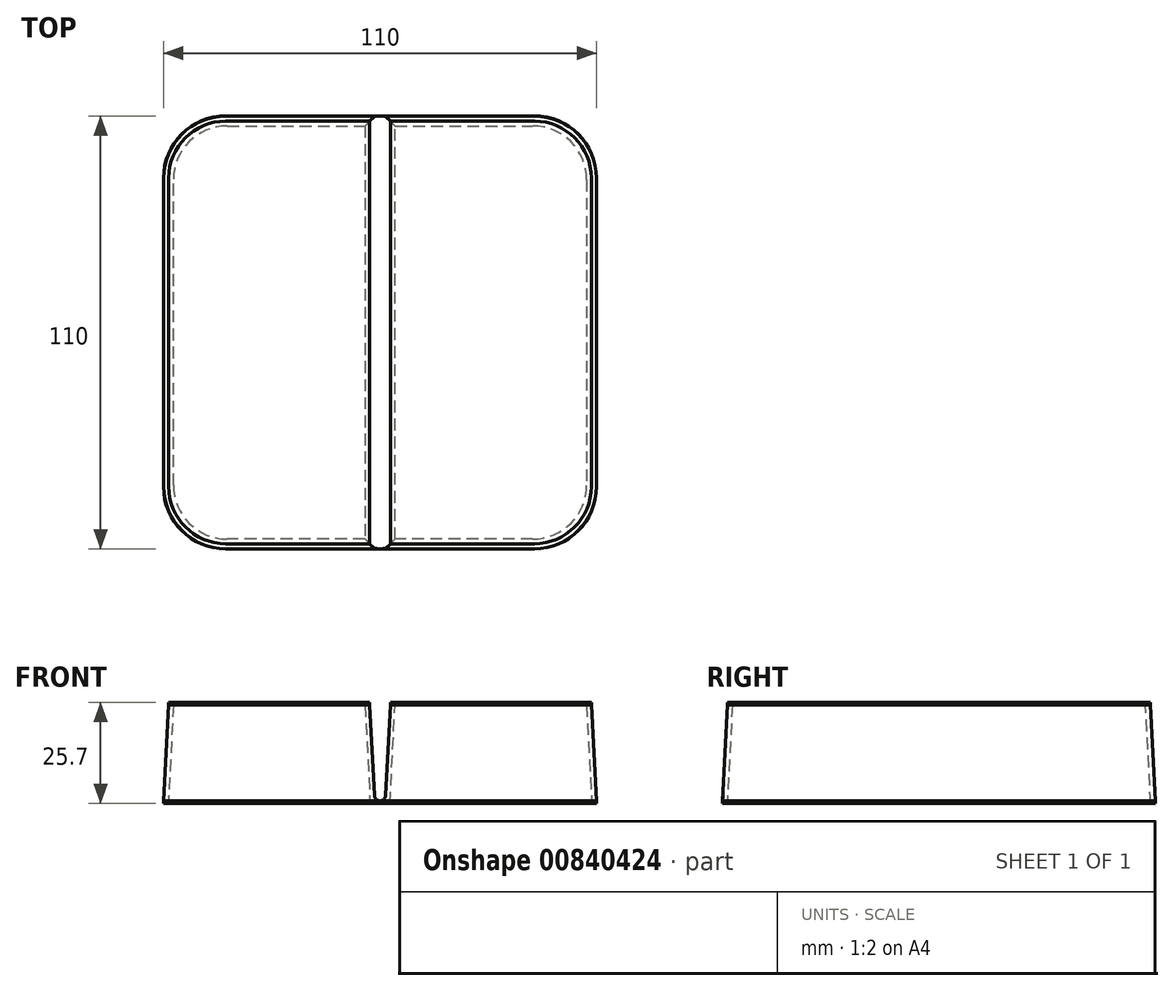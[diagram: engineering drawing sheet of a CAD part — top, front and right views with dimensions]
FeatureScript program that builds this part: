
annotation { "Feature Type Name" : "Feature", "Feature Type Description" : "" }
export const myFeature = defineFeature(function(context is Context, id is Id, definition is map)
    precondition{}
    {
        {
            var Q0;
            Q0=qCreatedBy(makeId("Top.planeOp"),FACE);
            var sketch = newSketch(context, id + "F0", { "sketchPlane" : qUnion([Q0])});
            skLineSegment(sketch, "E0.bottom", {"start": v(-39.2, 55) * mm, "end": v(39.2, 55) * mm});
            skLineSegment(sketch, "E0.top", {"start": v(-39.2, -55) * mm, "end": v(39.2, -55) * mm});
            skLineSegment(sketch, "E0.left", {"start": v(-55, 39.2) * mm, "end": v(-55, -39.2) * mm});
            skLineSegment(sketch, "E0.right", {"start": v(55, 39.2) * mm, "end": v(55, -39.2) * mm});
            skPoint(sketch, "E0.middle", {"position": v(0, 0) * mm});
            skLineSegment(sketch, "E1.bottom", {"start": v(39.2, 65) * mm, "end": v(-39.2, 65) * mm});
            skLineSegment(sketch, "E1.top", {"start": v(39.2, -65) * mm, "end": v(-39.2, -65) * mm});
            skLineSegment(sketch, "E1.left", {"start": v(65, 39.2) * mm, "end": v(65, -39.2) * mm});
            skLineSegment(sketch, "E1.right", {"start": v(-65, 39.2) * mm, "end": v(-65, -39.2) * mm});
            skLineSegment(sketch, "E2.0", {"start": v(-38.8, 53.8) * mm, "end": v(38.8, 53.8) * mm});
            skLineSegment(sketch, "E2.1", {"start": v(-53.8, 38.8) * mm, "end": v(-53.8, -38.8) * mm});
            skLineSegment(sketch, "E2.2", {"start": v(-38.8, -53.8) * mm, "end": v(38.8, -53.8) * mm});
            skLineSegment(sketch, "E2.3", {"start": v(53.8, 38.8) * mm, "end": v(53.8, -38.8) * mm});
            skPoint(sketch, "E3.visualSharp", {"position": v(-53.8, -53.8) * mm});
            skArc(sketch, "E3.filletArc", {"start": v(-53.8, -38.8) * mm, "mid": v(-49.4, -49.4) * mm, "end": v(-38.8, -53.8) * mm});
            skPoint(sketch, "E4.visualSharp", {"position": v(-55, -55) * mm});
            skArc(sketch, "E4.filletArc", {"start": v(-55, -39.2) * mm, "mid": v(-50.37, -50.37) * mm, "end": v(-39.2, -55) * mm});
            skPoint(sketch, "E5.visualSharp", {"position": v(53.8, -53.8) * mm});
            skArc(sketch, "E5.filletArc", {"start": v(38.8, -53.8) * mm, "mid": v(49.4, -49.4) * mm, "end": v(53.8, -38.8) * mm});
            skPoint(sketch, "E6.visualSharp", {"position": v(53.8, 53.8) * mm});
            skArc(sketch, "E6.filletArc", {"start": v(53.8, 38.8) * mm, "mid": v(49.4, 49.4) * mm, "end": v(38.8, 53.8) * mm});
            skPoint(sketch, "E7.visualSharp", {"position": v(-53.8, 53.8) * mm});
            skArc(sketch, "E7.filletArc", {"start": v(-38.8, 53.8) * mm, "mid": v(-49.4, 49.4) * mm, "end": v(-53.8, 38.8) * mm});
            skPoint(sketch, "E8.visualSharp", {"position": v(-55, 55) * mm});
            skArc(sketch, "E8.filletArc", {"start": v(-39.2, 55) * mm, "mid": v(-50.37, 50.37) * mm, "end": v(-55, 39.2) * mm});
            skPoint(sketch, "E9.visualSharp", {"position": v(55, 55) * mm});
            skArc(sketch, "E9.filletArc", {"start": v(55, 39.2) * mm, "mid": v(50.37, 50.37) * mm, "end": v(39.2, 55) * mm});
            skPoint(sketch, "E10.visualSharp", {"position": v(55, -55) * mm});
            skArc(sketch, "E10.filletArc", {"start": v(39.2, -55) * mm, "mid": v(50.37, -50.37) * mm, "end": v(55, -39.2) * mm});
            skPoint(sketch, "E11.visualSharp", {"position": v(65, -65) * mm});
            skArc(sketch, "E11.filletArc", {"start": v(39.2, -65) * mm, "mid": v(57.44, -57.44) * mm, "end": v(65, -39.2) * mm});
            skPoint(sketch, "E12.visualSharp", {"position": v(-65, -65) * mm});
            skArc(sketch, "E12.filletArc", {"start": v(-65, -39.2) * mm, "mid": v(-57.44, -57.44) * mm, "end": v(-39.2, -65) * mm});
            skPoint(sketch, "E13.visualSharp", {"position": v(65, 65) * mm});
            skArc(sketch, "E13.filletArc", {"start": v(65, 39.2) * mm, "mid": v(57.44, 57.44) * mm, "end": v(39.2, 65) * mm});
            skPoint(sketch, "E14.visualSharp", {"position": v(-65, 65) * mm});
            skArc(sketch, "E14.filletArc", {"start": v(-39.2, 65) * mm, "mid": v(-57.44, 57.44) * mm, "end": v(-65, 39.2) * mm});
            skLineSegment(sketch, "E15.0", {"start": v(60, 35.37) * mm, "end": v(60, -43.03) * mm});
            skLineSegment(sketch, "E16.0", {"start": v(-60, 35.37) * mm, "end": v(-60, -43.03) * mm});
            skCircle(sketch, "E17", {"center": v(60, 35.37) * mm, "radius": 2.1 * mm});
            skCircle(sketch, "E18", {"center": v(60, -43.03) * mm, "radius": 2.1 * mm});
            skCircle(sketch, "E19", {"center": v(-60, 35.37) * mm, "radius": 2.1 * mm});
            skCircle(sketch, "E20", {"center": v(-60, -43.03) * mm, "radius": 2.1 * mm});
            skLineSegment(sketch, "E21.0", {"start": v(39.2, 60) * mm, "end": v(-39.2, 60) * mm});
            skCircle(sketch, "E22", {"center": v(-39.2, 60) * mm, "radius": 2.1 * mm});
            skCircle(sketch, "E23", {"center": v(39.2, 60) * mm, "radius": 2.1 * mm});
            skLineSegment(sketch, "E24", {"start": v(-2.5, -55) * mm, "end": v(-2.5, 55) * mm});
            skLineSegment(sketch, "E25", {"start": v(2.5, 55) * mm, "end": v(2.5, -55) * mm});
            skLineSegment(sketch, "E26.0", {"start": v(1.3, 55) * mm, "end": v(1.3, -55) * mm});
            skLineSegment(sketch, "E27.0", {"start": v(-1.3, -55) * mm, "end": v(-1.3, 55) * mm});
            skSolve(sketch);
        }
        {
            var Q0;
            Q0=makeQuery(id+"F0.imprint","IMPRINT",FACE,{"disambiguationData":[TD([[makeQuery(id+"F0.imprint","IMPRINT",EDGE,{"derivedFrom":sQuery(id+"F0.wireOp",EDGE,"E0.bottom")}),-1.0]])]});
            var Q1;
            {var subQ0=sQuery(id+"F0.wireOp",EDGE,"E24");Q1=makeQuery(id+"F0.imprint","IMPRINT",FACE,{"disambiguationData":[TD([[makeQuery(id+"F0.imprint","IMPRINT",EDGE,{"derivedFrom":subQ0}),-1.0]])]});}
            var Q2;
            {var subQ0=sQuery(id+"F0.wireOp",EDGE,"E25");var subQ1=sQuery(id+"F0.wireOp",EDGE,"E2.0");var subQ2=makeQuery(id+"F0.imprint","INTERSECT",VERTEX,{"derivedFrom":[subQ1,subQ0]});Q2=makeQuery(id+"F0.imprint","IMPRINT",FACE,{"disambiguationData":[TD([[makeQuery(id+"F0.imprint","IMPRINT",EDGE,{"disambiguationData":[TD([[subQ2,1.0]])],"derivedFrom":subQ1}),-1.0]])]});}
            var Q3;
            {var subQ3=sQuery(id+"F0.wireOp",EDGE,"E27.0");Q3=makeQuery(id+"F0.imprint","IMPRINT",FACE,{"disambiguationData":[TD([[makeQuery(id+"F0.imprint","IMPRINT",EDGE,{"derivedFrom":subQ3}),-1.0]])]});}
            var Q4;
            {var subQ0=sQuery(id+"F0.wireOp",EDGE,"E25");var subQ1=sQuery(id+"F0.wireOp",EDGE,"E0.top");var subQ2=makeQuery(id+"F0.imprint","INTERSECT",VERTEX,{"derivedFrom":[subQ1,subQ0]});Q4=makeQuery(id+"F0.imprint","IMPRINT",FACE,{"disambiguationData":[TD([[makeQuery(id+"F0.imprint","IMPRINT",EDGE,{"disambiguationData":[TD([[subQ2,1.0]])],"derivedFrom":subQ1}),1.0]])]});}
            var Q5;
            Q5=makeQuery(id+"F0.imprint","IMPRINT",FACE,{"disambiguationData":[TD([[makeQuery(id+"F0.imprint","IMPRINT",EDGE,{"derivedFrom":sQuery(id+"F0.wireOp",EDGE,"E0.right")}),-1.0]])]});
            var Q6;
            Q6=makeQuery(id+"F0.imprint","IMPRINT",FACE,{"disambiguationData":[TD([[makeQuery(id+"F0.imprint","IMPRINT",EDGE,{"derivedFrom":sQuery(id+"F0.wireOp",EDGE,"E0.left")}),1.0]])]});
            extrude(context, id + "F1", {"entities" : qUnion([Q0, Q1, Q2, Q3, Q4, Q5, Q6]), "depth" : 0.7 * mm, "offsetDistance" : 25 * mm});
        }
        {
            var Q0;
            {var subQ0=sQuery(id+"F0.wireOp",EDGE,"E25");var subQ1=sQuery(id+"F0.wireOp",EDGE,"E0.bottom");var subQ2=makeQuery(id+"F0.imprint","INTERSECT",VERTEX,{"derivedFrom":[subQ1,subQ0]});Q0=makeQuery(id+"F0.imprint","IMPRINT",FACE,{"disambiguationData":[TD([[makeQuery(id+"F0.imprint","IMPRINT",EDGE,{"disambiguationData":[TD([[subQ2,1.0]])],"derivedFrom":subQ1}),-1.0]])]});}
            var Q1;
            {var subQ0=sQuery(id+"F0.wireOp",EDGE,"E25");var subQ1=sQuery(id+"F0.wireOp",EDGE,"E0.top");var subQ2=makeQuery(id+"F0.imprint","INTERSECT",VERTEX,{"derivedFrom":[subQ1,subQ0]});Q1=makeQuery(id+"F0.imprint","IMPRINT",FACE,{"disambiguationData":[TD([[makeQuery(id+"F0.imprint","IMPRINT",EDGE,{"disambiguationData":[TD([[subQ2,1.0]])],"derivedFrom":subQ1}),1.0]])]});}
            var Q2;
            {var subQ0=sQuery(id+"F0.wireOp",EDGE,"E26.0");var subQ1=sQuery(id+"F0.wireOp",EDGE,"E2.0");var subQ2=makeQuery(id+"F0.imprint","INTERSECT",VERTEX,{"derivedFrom":[subQ1,subQ0]});Q2=makeQuery(id+"F0.imprint","IMPRINT",FACE,{"disambiguationData":[TD([[makeQuery(id+"F0.imprint","IMPRINT",EDGE,{"disambiguationData":[TD([[subQ2,-1.0]])],"derivedFrom":subQ1}),-1.0]])]});}
            var Q3;
            Q3=makeQuery(id+"F0.imprint","IMPRINT",FACE,{"disambiguationData":[TD([[makeQuery(id+"F0.imprint","IMPRINT",EDGE,{"derivedFrom":sQuery(id+"F0.wireOp",EDGE,"E0.right")}),-1.0]])]});
            var Q4;
            Q4=makeQuery(id+"F0.imprint","IMPRINT",FACE,{"disambiguationData":[TD([[makeQuery(id+"F0.imprint","IMPRINT",EDGE,{"derivedFrom":sQuery(id+"F0.wireOp",EDGE,"E2.3")}),-1.0]])]});
            var Q5;
            {var subQ0=sQuery(id+"F0.wireOp",EDGE,"E24");var subQ1=sQuery(id+"F0.wireOp",EDGE,"E2.0");var subQ2=makeQuery(id+"F0.imprint","INTERSECT",VERTEX,{"derivedFrom":[subQ1,subQ0]});Q5=makeQuery(id+"F0.imprint","IMPRINT",FACE,{"disambiguationData":[TD([[makeQuery(id+"F0.imprint","IMPRINT",EDGE,{"disambiguationData":[TD([[subQ2,-1.0]])],"derivedFrom":subQ1}),-1.0]])]});}
            var Q6;
            {var subQ0=sQuery(id+"F0.wireOp",EDGE,"E24");var subQ1=sQuery(id+"F0.wireOp",EDGE,"E0.top");var subQ2=makeQuery(id+"F0.imprint","INTERSECT",VERTEX,{"derivedFrom":[subQ1,subQ0]});Q6=makeQuery(id+"F0.imprint","IMPRINT",FACE,{"disambiguationData":[TD([[makeQuery(id+"F0.imprint","IMPRINT",EDGE,{"disambiguationData":[TD([[subQ2,-1.0]])],"derivedFrom":subQ1}),1.0]])]});}
            var Q7;
            Q7=makeQuery(id+"F0.imprint","IMPRINT",FACE,{"disambiguationData":[TD([[makeQuery(id+"F0.imprint","IMPRINT",EDGE,{"derivedFrom":sQuery(id+"F0.wireOp",EDGE,"E0.left")}),1.0]])]});
            var Q8;
            {var subQ0=sQuery(id+"F0.wireOp",EDGE,"E24");var subQ1=sQuery(id+"F0.wireOp",EDGE,"E0.bottom");var subQ2=makeQuery(id+"F0.imprint","INTERSECT",VERTEX,{"derivedFrom":[subQ1,subQ0]});Q8=makeQuery(id+"F0.imprint","IMPRINT",FACE,{"disambiguationData":[TD([[makeQuery(id+"F0.imprint","IMPRINT",EDGE,{"disambiguationData":[TD([[subQ2,-1.0]])],"derivedFrom":subQ1}),-1.0]])]});}
            var Q9;
            Q9=makeQuery(id+"F0.imprint","IMPRINT",FACE,{"disambiguationData":[TD([[makeQuery(id+"F0.imprint","IMPRINT",EDGE,{"derivedFrom":sQuery(id+"F0.wireOp",EDGE,"E2.1")}),1.0]])]});
            extrude(context, id + "F2", {"entities" : qUnion([Q0, Q1, Q2, Q3, Q4, Q5, Q6, Q7, Q8, Q9]), "operationType" : NewBodyOperationType.ADD, "depth" : 25 * mm, "offsetDistance" : 25 * mm, "hasDraft" : true, "draftAngle" : 3 * degree, "draftPullDirection" : true});
        }
        {
            var Q0;
            Q0=makeQuery(id+"F0.imprint","IMPRINT",FACE,{"disambiguationData":[TD([[makeQuery(id+"F0.imprint","IMPRINT",EDGE,{"derivedFrom":sQuery(id+"F0.wireOp",EDGE,"E2.1")}),1.0]])]});
            var Q1;
            Q1=makeQuery(id+"F0.imprint","IMPRINT",FACE,{"disambiguationData":[TD([[makeQuery(id+"F0.imprint","IMPRINT",EDGE,{"derivedFrom":sQuery(id+"F0.wireOp",EDGE,"E2.3")}),-1.0]])]});
            extrude(context, id + "F3", {"entities" : qUnion([Q0, Q1]), "operationType" : NewBodyOperationType.REMOVE, "depth" : 25 * mm, "offsetDistance" : 25 * mm, "hasDraft" : true, "draftAngle" : 3 * degree, "draftPullDirection" : true});
        }
        {
            var Q0;
            Q0=makeQuery(id+"F2.opExtrude","CAP_FACE",FACE,{"disambiguationData":[OSD([sQuery(id+"F0.wireOp",EDGE,"E0.bottom"),sQuery(id+"F0.wireOp",EDGE,"E0.top"),sQuery(id+"F0.wireOp",EDGE,"E0.right"),sQuery(id+"F0.wireOp",EDGE,"E9.filletArc"),sQuery(id+"F0.wireOp",EDGE,"E10.filletArc"),sQuery(id+"F0.wireOp",EDGE,"E26.0")])],"isStart":false});
            var sketch = newSketch(context, id + "F4", { "sketchPlane" : qUnion([Q0])});
            skLineSegment(sketch, "E28.0", {"start": v(2.61, 53.69) * mm, "end": v(2.61, -53.69) * mm});
            skLineSegment(sketch, "E29.0", {"start": v(2.61, -53.69) * mm, "end": v(39.2, -53.69) * mm});
            skArc(sketch, "E30.0", {"start": v(39.2, -53.69) * mm, "mid": v(49.45, -49.45) * mm, "end": v(53.69, -39.2) * mm});
            skLineSegment(sketch, "E31.0", {"start": v(53.69, 39.2) * mm, "end": v(53.69, -39.2) * mm});
            skLineSegment(sketch, "E32.0", {"start": v(2.61, 53.69) * mm, "end": v(39.2, 53.69) * mm});
            skArc(sketch, "E33.0", {"start": v(53.69, 39.2) * mm, "mid": v(49.45, 49.45) * mm, "end": v(39.2, 53.69) * mm});
            skSolve(sketch);
        }
        {
            var Q0;
            Q0 = qSketchRegion(id + "F4", true);
            extrude(context, id + "F5", {"entities" : qUnion([Q0]), "operationType" : NewBodyOperationType.ADD, "depth" : 0.7 * mm, "offsetDistance" : 25 * mm});
        }
        {
            var Q0;
            Q0=makeQuery(id+"F2.opExtrude","CAP_FACE",FACE,{"disambiguationData":[OSD([sQuery(id+"F0.wireOp",EDGE,"E0.bottom"),sQuery(id+"F0.wireOp",EDGE,"E0.top"),sQuery(id+"F0.wireOp",EDGE,"E0.left"),sQuery(id+"F0.wireOp",EDGE,"E4.filletArc"),sQuery(id+"F0.wireOp",EDGE,"E8.filletArc"),sQuery(id+"F0.wireOp",EDGE,"E27.0")])],"isStart":false});
            var sketch = newSketch(context, id + "F6", { "sketchPlane" : qUnion([Q0])});
            skLineSegment(sketch, "E34.0", {"start": v(-2.61, -53.69) * mm, "end": v(-2.61, 53.69) * mm});
            skLineSegment(sketch, "E35.0", {"start": v(-39.2, -53.69) * mm, "end": v(-2.61, -53.69) * mm});
            skArc(sketch, "E36.0", {"start": v(-53.69, -39.2) * mm, "mid": v(-49.45, -49.45) * mm, "end": v(-39.2, -53.69) * mm});
            skLineSegment(sketch, "E37.0", {"start": v(-53.69, 39.2) * mm, "end": v(-53.69, -39.2) * mm});
            skArc(sketch, "E38.0", {"start": v(-39.2, 53.69) * mm, "mid": v(-49.45, 49.45) * mm, "end": v(-53.69, 39.2) * mm});
            skLineSegment(sketch, "E39.0", {"start": v(-39.2, 53.69) * mm, "end": v(-2.61, 53.69) * mm});
            skSolve(sketch);
        }
        {
            var Q0;
            Q0 = qSketchRegion(id + "F6", true);
            extrude(context, id + "F7", {"entities" : qUnion([Q0]), "operationType" : NewBodyOperationType.ADD, "depth" : 0.7 * mm, "offsetDistance" : 25 * mm});
        }
        {
            var Q0;
            Q0=makeQuery(id+"F2.boolean.opBoolean","INTERSECT",EDGE,{"derivedFrom":[makeQuery(id+"F1.opExtrude","CAP_FACE",FACE,{"disambiguationData":[OSD([sQuery(id+"F0.wireOp",EDGE,"E0.bottom"),sQuery(id+"F0.wireOp",EDGE,"E0.top"),sQuery(id+"F0.wireOp",EDGE,"E0.left"),sQuery(id+"F0.wireOp",EDGE,"E0.right"),sQuery(id+"F0.wireOp",EDGE,"E2.0"),sQuery(id+"F0.wireOp",EDGE,"E2.1"),sQuery(id+"F0.wireOp",EDGE,"E2.2"),sQuery(id+"F0.wireOp",EDGE,"E2.3"),sQuery(id+"F0.wireOp",EDGE,"E3.filletArc"),sQuery(id+"F0.wireOp",EDGE,"E4.filletArc"),sQuery(id+"F0.wireOp",EDGE,"E5.filletArc"),sQuery(id+"F0.wireOp",EDGE,"E6.filletArc"),sQuery(id+"F0.wireOp",EDGE,"E7.filletArc"),sQuery(id+"F0.wireOp",EDGE,"E8.filletArc"),sQuery(id+"F0.wireOp",EDGE,"E9.filletArc"),sQuery(id+"F0.wireOp",EDGE,"E10.filletArc"),sQuery(id+"F0.wireOp",EDGE,"E24"),sQuery(id+"F0.wireOp",EDGE,"E25")])],"isStart":false}),makeQuery(id+"F2.opExtrude","SWEPT_FACE",FACE,{"disambiguationData":[OSD([sQuery(id+"F0.wireOp",EDGE,"E26.0")])]})]});
            var Q1;
            Q1=makeQuery(id+"F2.boolean.opBoolean","INTERSECT",EDGE,{"derivedFrom":[makeQuery(id+"F1.opExtrude","CAP_FACE",FACE,{"disambiguationData":[OSD([sQuery(id+"F0.wireOp",EDGE,"E0.bottom"),sQuery(id+"F0.wireOp",EDGE,"E0.top"),sQuery(id+"F0.wireOp",EDGE,"E0.left"),sQuery(id+"F0.wireOp",EDGE,"E0.right"),sQuery(id+"F0.wireOp",EDGE,"E2.0"),sQuery(id+"F0.wireOp",EDGE,"E2.1"),sQuery(id+"F0.wireOp",EDGE,"E2.2"),sQuery(id+"F0.wireOp",EDGE,"E2.3"),sQuery(id+"F0.wireOp",EDGE,"E3.filletArc"),sQuery(id+"F0.wireOp",EDGE,"E4.filletArc"),sQuery(id+"F0.wireOp",EDGE,"E5.filletArc"),sQuery(id+"F0.wireOp",EDGE,"E6.filletArc"),sQuery(id+"F0.wireOp",EDGE,"E7.filletArc"),sQuery(id+"F0.wireOp",EDGE,"E8.filletArc"),sQuery(id+"F0.wireOp",EDGE,"E9.filletArc"),sQuery(id+"F0.wireOp",EDGE,"E10.filletArc"),sQuery(id+"F0.wireOp",EDGE,"E24"),sQuery(id+"F0.wireOp",EDGE,"E25")])],"isStart":false}),makeQuery(id+"F2.opExtrude","SWEPT_FACE",FACE,{"disambiguationData":[OSD([sQuery(id+"F0.wireOp",EDGE,"E27.0")])]})]});
            fillet(context, id + "F8", {"entities" : qUnion([Q0, Q1]), "radius" : 1.4 * mm, "tangentPropagation" : true, "allowEdgeOverflow" : false});
        }
    });
